# Revit family: 4c66217e-2b51-4837-ba72-46877788c5ca
name_source: partatom
category: Specialty Equipment
revit_build: Autodesk Revit 2016 (Build: 20161004_0715(x64)
units: mm (PartAtom-declared; Revit-internal decimal feet)

## family parameters
Cut with Voids When Loaded = No
Host = Face
Part Type = Normal
Room Calculation Point = No
Round Connector Dimension = Use Diameter
Shared = No

## types (1)
- Paper Towel Dispenser - PH240
    ADA Compliant = ADA Compliant
    Default Elevation = 4' - 0"
    Description = The PH240 ligature resistant paper towel dispenser is a patent pending design which includes unique features that make it ideal for patient bathrooms or public areas in behavioral settings that necessitate ligature resistant products.
    Elevation (default) = 5' - 0"
    Grab Bar Height = 0' - 0"
    Grab Bar Length = 0' - 0"
    Installation instructions = https://besafeprod.com
    Manufacturer = Behavioral Safety Products
    Manufacturer Fax = 706.705.1191
    Material = Polycarbonate - BSP - White
    Model = PH240
    Product Page URL = https://besafeprod.com
    Spec Sheet URL = https://besafeprod.com
    SubCategory = Towel Dispenser
    Type Image = <None>
    URL = https://besafeprod.com

## geometry (parser evidence)
native form markers: Blend x2, Sweep x3
no freeform markers — native parametric forms only
